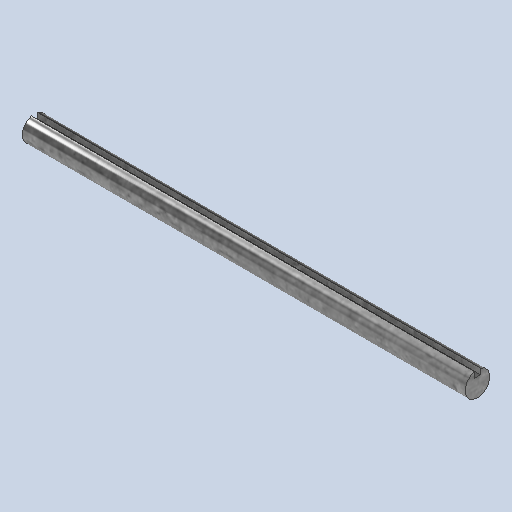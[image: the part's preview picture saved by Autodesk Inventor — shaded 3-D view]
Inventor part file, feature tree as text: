
AUTODESK INVENTOR PART (.ipt)
format: ipt  version: 2023 (Build 270158000, 158)  size: 113,152 bytes
history: native  units: in
note: dims shown in document units (in); Inventor stores cm internally (conversion verified against a paired STEP export)
features: other x3, sketch x1
ambient origin geometry x8: Origin, YZ Plane, XZ Plane, XY Plane, X Axis, Y Axis, Z Axis, Center Point
bodies: Solid1 (feature_tree)
feature tree (4):
  other  "SteelDeadAxel.ipt"
  other  "Solid1::SteelDeadAxel.ipt"
  other  "TaggingFeature1"
  sketch  "Sketch1"  dims[d0=0.3937in]
